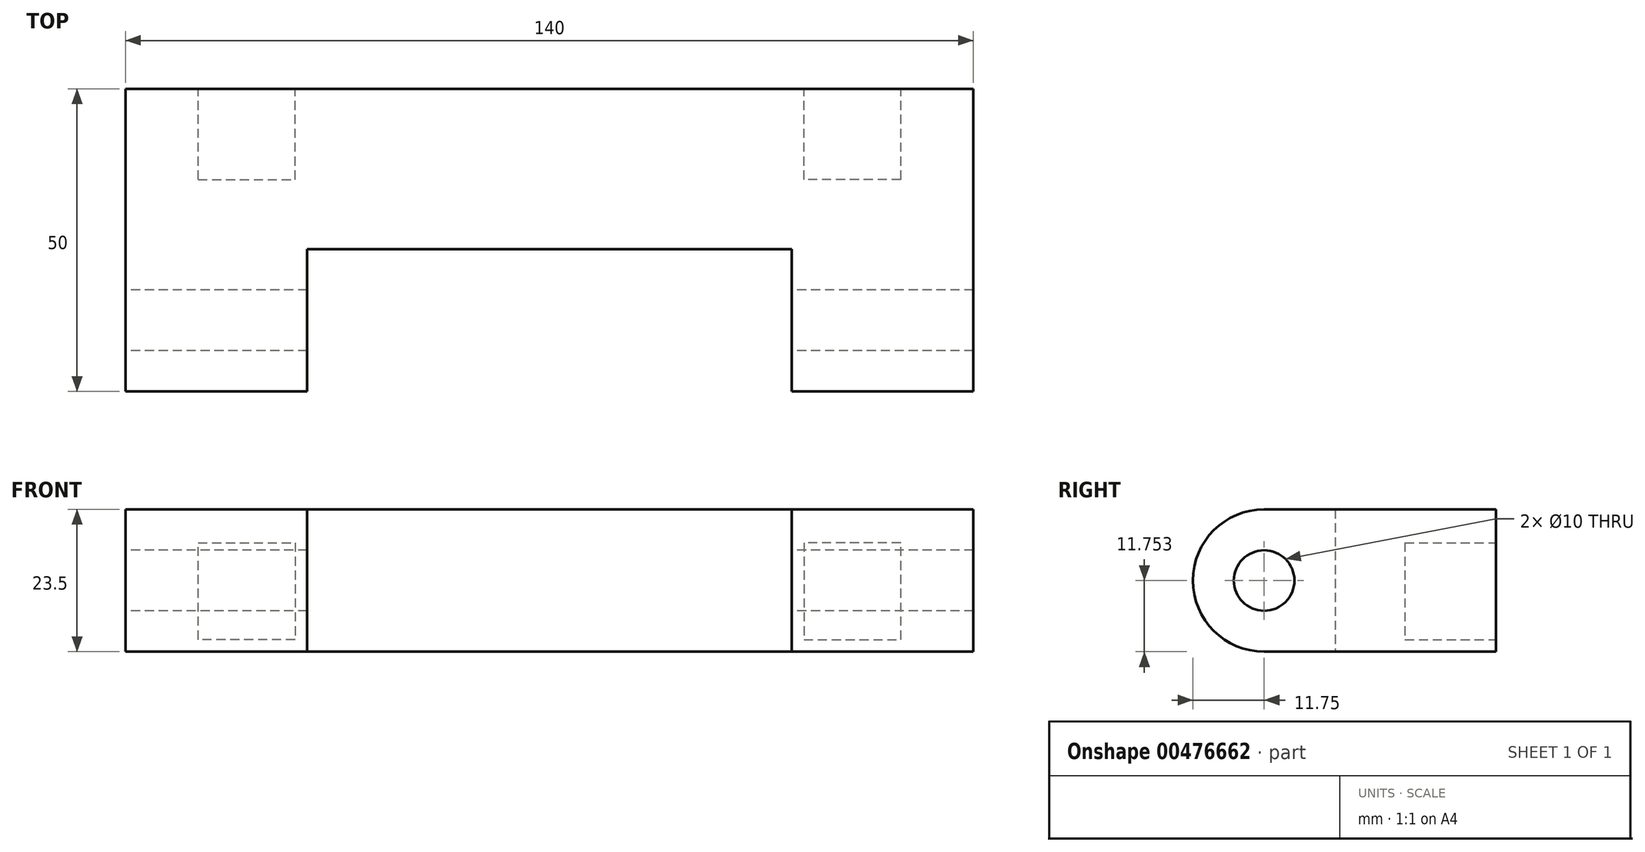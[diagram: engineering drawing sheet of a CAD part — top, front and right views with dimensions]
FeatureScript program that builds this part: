
annotation { "Feature Type Name" : "Feature", "Feature Type Description" : "" }
export const myFeature = defineFeature(function(context is Context, id is Id, definition is map)
    precondition{}
    {
        {
            var Q0;
            Q0=qCreatedBy(makeId("Front.planeOp"),FACE);
            var sketch = newSketch(context, id + "F0", { "sketchPlane" : qUnion([Q0])});
            skLineSegment(sketch, "E0.bottom", {"start": v(61.27, -8.09) * mm, "end": v(-78.73, -8.09) * mm});
            skLineSegment(sketch, "E0.top", {"start": v(61.27, -31.59) * mm, "end": v(-78.73, -31.59) * mm});
            skLineSegment(sketch, "E0.left", {"start": v(61.27, -8.09) * mm, "end": v(61.27, -31.59) * mm});
            skLineSegment(sketch, "E0.right", {"start": v(-78.73, -8.09) * mm, "end": v(-78.73, -31.59) * mm});
            skSolve(sketch);
        }
        {
            var Q0;
            Q0 = qSketchRegion(id + "F0", true);
            extrude(context, id + "F1", {"entities" : qUnion([Q0]), "depth" : 50 * mm});
        }
        {
            var Q0;
            Q0=makeQuery(id+"F1.opExtrude","CAP_FACE",FACE,{"disambiguationData":[OSD([sQuery(id+"F0.wireOp",EDGE,"E0.bottom"),sQuery(id+"F0.wireOp",EDGE,"E0.top"),sQuery(id+"F0.wireOp",EDGE,"E0.left"),sQuery(id+"F0.wireOp",EDGE,"E0.right")])],"isStart":true});
            var sketch = newSketch(context, id + "F2", { "sketchPlane" : qUnion([Q0])});
            skPoint(sketch, "E1.startSnap0", {"position": v(8.73, -31.59) * mm});
            skLineSegment(sketch, "E2", {"start": v(-33.27, -13.59) * mm, "end": v(-33.27, -29.59) * mm});
            skLineSegment(sketch, "E3", {"start": v(-33.27, -29.59) * mm, "end": v(-49.27, -29.59) * mm});
            skLineSegment(sketch, "E4", {"start": v(-49.27, -29.59) * mm, "end": v(-49.27, -13.59) * mm});
            skLineSegment(sketch, "E5", {"start": v(-49.27, -13.59) * mm, "end": v(-33.27, -13.59) * mm});
            skPoint(sketch, "E6.endSnap0", {"position": v(8.73, -8.09) * mm});
            skLineSegment(sketch, "E7.MirrorCS", {"start": v(50.73, -13.59) * mm, "end": v(50.73, -29.59) * mm});
            skLineSegment(sketch, "E8.MirrorCS", {"start": v(66.73, -13.59) * mm, "end": v(50.73, -13.59) * mm});
            skLineSegment(sketch, "E9.MirrorCS", {"start": v(66.73, -29.59) * mm, "end": v(66.73, -13.59) * mm});
            skLineSegment(sketch, "E10.MirrorCS", {"start": v(50.73, -29.59) * mm, "end": v(66.73, -29.59) * mm});
            skSolve(sketch);
        }
        {
            var Q0;
            Q0=makeQuery(id+"F2.imprint","IMPRINT",FACE,{"disambiguationData":[TD([[makeQuery(id+"F2.imprint","IMPRINT",EDGE,{"derivedFrom":sQuery(id+"F2.wireOp",EDGE,"E2")}),-1.0]])]});
            var Q1;
            Q1=makeQuery(id+"F2.imprint","IMPRINT",FACE,{"disambiguationData":[TD([[makeQuery(id+"F2.imprint","IMPRINT",EDGE,{"derivedFrom":sQuery(id+"F2.wireOp",EDGE,"E7.MirrorCS")}),1.0]])]});
            extrude(context, id + "F3", {"entities" : qUnion([Q0, Q1]), "operationType" : NewBodyOperationType.REMOVE, "oppositeDirection" : true, "depth" : 15 * mm});
        }
        {
            var Q0;
            Q0=makeQuery(id+"F1.opExtrude","CAP_EDGE",EDGE,{"disambiguationData":[OSD([sQuery(id+"F0.wireOp",EDGE,"E0.bottom")])],"isStart":false});
            var Q1;
            Q1=makeQuery(id+"F1.opExtrude","CAP_EDGE",EDGE,{"disambiguationData":[OSD([sQuery(id+"F0.wireOp",EDGE,"E0.top")])],"isStart":false});
            fillet(context, id + "F4", {"entities" : qUnion([Q0, Q1]), "radius" : 11.75 * mm, "tangentPropagation" : true, "allowEdgeOverflow" : false});
        }
        {
            var Q0;
            Q0=makeQuery(id+"F1.opExtrude","SWEPT_FACE",FACE,{"disambiguationData":[OSD([sQuery(id+"F0.wireOp",EDGE,"E0.right")])]});
            var sketch = newSketch(context, id + "F5", { "sketchPlane" : qUnion([Q0])});
            skCircle(sketch, "E11", {"center": v(38.25, -19.84) * mm, "radius": 5 * mm});
            skSolve(sketch);
        }
        {
            var Q0;
            Q0=makeQuery(id+"F5.imprint","IMPRINT",FACE,{"disambiguationData":[TD([[makeQuery(id+"F5.imprint","IMPRINT",EDGE,{"derivedFrom":sQuery(id+"F5.wireOp",EDGE,"E11")}),1.0]])]});
            extrude(context, id + "F6", {"entities" : qUnion([Q0]), "operationType" : NewBodyOperationType.REMOVE, "endBound" : BoundingType.UP_TO_NEXT, "oppositeDirection" : true, "depth" : 25 * mm});
        }
        {
            var Q0;
            Q0=makeQuery(id+"F1.opExtrude","SWEPT_FACE",FACE,{"disambiguationData":[OSD([sQuery(id+"F0.wireOp",EDGE,"E0.top")])]});
            var sketch = newSketch(context, id + "F7", { "sketchPlane" : qUnion([Q0])});
            skLineSegment(sketch, "E12", {"start": v(-78.73, 38.25) * mm, "end": v(-78.73, 33.25) * mm});
            skLineSegment(sketch, "E13", {"start": v(-78.73, 33.25) * mm, "end": v(-78.73, 26.5) * mm});
            skPoint(sketch, "E14.firstSnap0", {"position": v(-8.73, 38.25) * mm});
            skLineSegment(sketch, "E14.bottom", {"start": v(-8.73, 51.5) * mm, "end": v(-48.73, 51.5) * mm});
            skLineSegment(sketch, "E14.top", {"start": v(-8.73, 26.5) * mm, "end": v(-48.73, 26.5) * mm});
            skLineSegment(sketch, "E14.right", {"start": v(-48.73, 51.5) * mm, "end": v(-48.73, 26.5) * mm});
            skLineSegment(sketch, "E15.bottom", {"start": v(-48.73, 51.5) * mm, "end": v(31.27, 51.5) * mm});
            skLineSegment(sketch, "E15.top", {"start": v(-48.73, 26.5) * mm, "end": v(31.27, 26.5) * mm});
            skLineSegment(sketch, "E15.right", {"start": v(31.27, 51.5) * mm, "end": v(31.27, 26.5) * mm});
            skSolve(sketch);
        }
        {
            var Q0;
            Q0 = qSketchRegion(id + "F7", true);
            extrude(context, id + "F8", {"entities" : qUnion([Q0]), "operationType" : NewBodyOperationType.REMOVE, "oppositeDirection" : true, "depth" : 25 * mm});
        }
    });
